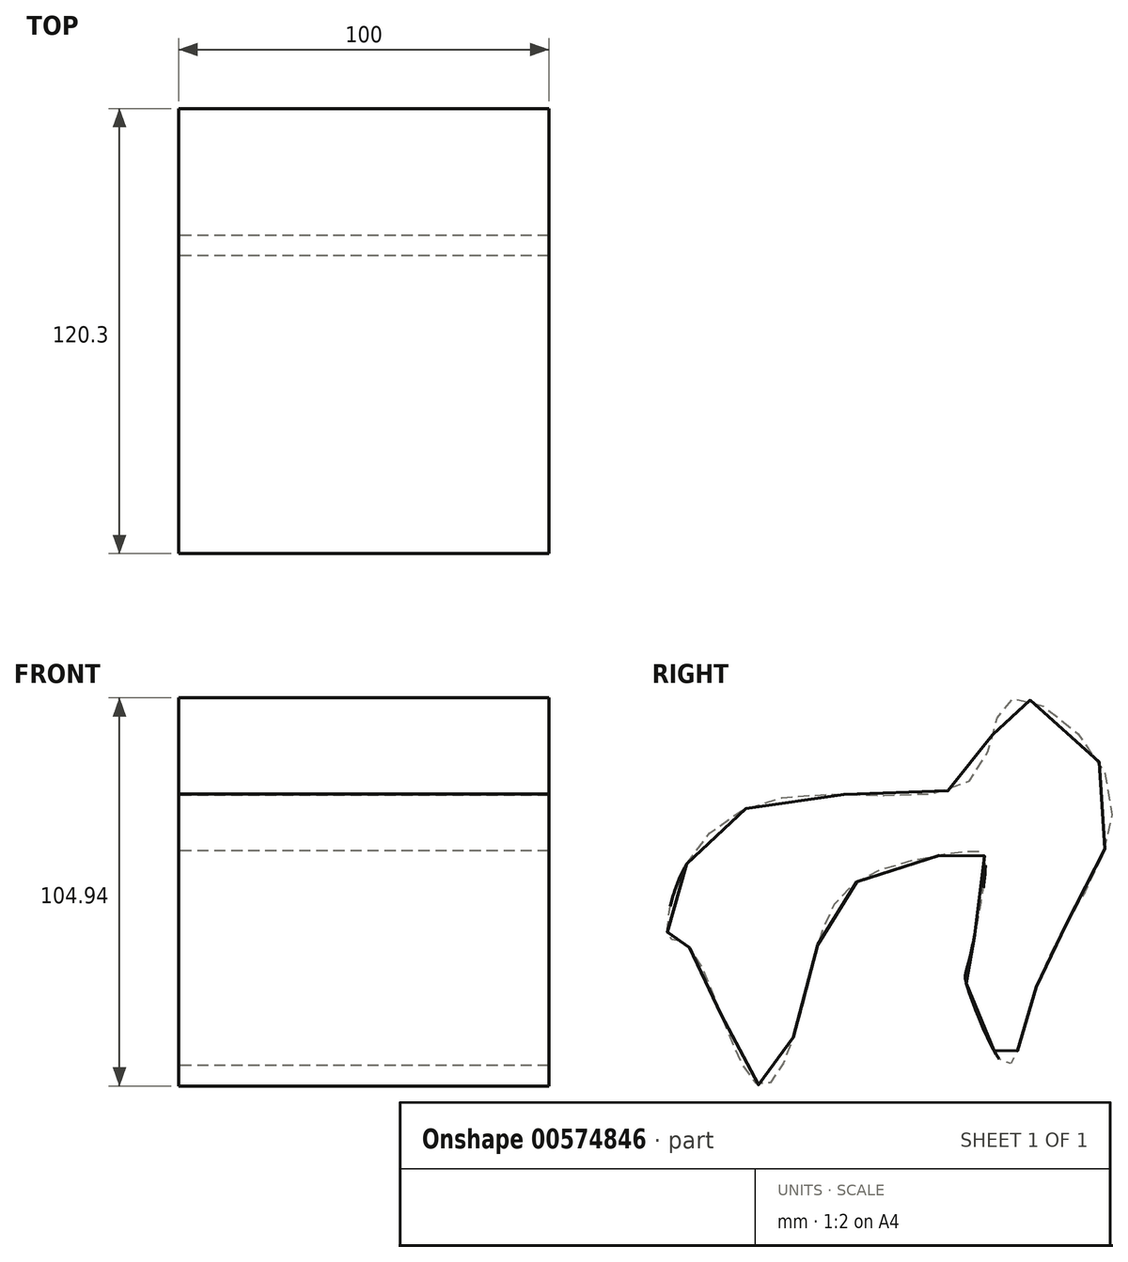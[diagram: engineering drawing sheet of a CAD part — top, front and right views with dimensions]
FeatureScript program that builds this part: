
annotation { "Feature Type Name" : "Feature", "Feature Type Description" : "" }
export const myFeature = defineFeature(function(context is Context, id is Id, definition is map)
    precondition{}
    {
        {
            var Q0;
            Q0=qCreatedBy(makeId("Right.planeOp"),FACE);
            var sketch = newSketch(context, id + "F0", { "sketchPlane" : qUnion([Q0])});
            skFitSpline(sketch, "E0", {"points": [v(-62.6, 9.07) * mm, v(-33.06, 27.53) * mm, v(15.25, 32.66) * mm, v(24.88, 53.53) * mm, v(51.04, 32.18) * mm, v(42.53, -2.97) * mm, v(31.3, -26.08) * mm, v(25.68, -44.22) * mm, v(23.11, -45.02) * mm, v(13.16, -23.67) * mm, v(13.32, -18.86) * mm, v(17.98, 11.15) * mm, v(13.96, 12.44) * mm, v(-17.01, 3.93) * mm, v(-30.17, -25.28) * mm, v(-42.37, -50.96) * mm, v(-57.3, -21.27) * mm, v(-64.36, -11.8) * mm, v(-67.25, -11) * mm, v(-62.6, 9.07) * mm]});
            skSolve(sketch);
        }
        {
            var Q0;
            Q0=makeQuery(id+"F0.imprint","IMPRINT",FACE,{"disambiguationData":[TD([[makeQuery(id+"F0.imprint","IMPRINT",EDGE,{"derivedFrom":sQuery(id+"F0.wireOp",EDGE,"E0")}),-1.0]])]});
            extrude(context, id + "F1", {"entities" : qUnion([Q0]), "depth" : 100 * mm, "offsetDistance" : 25.4 * mm});
        }
    });
